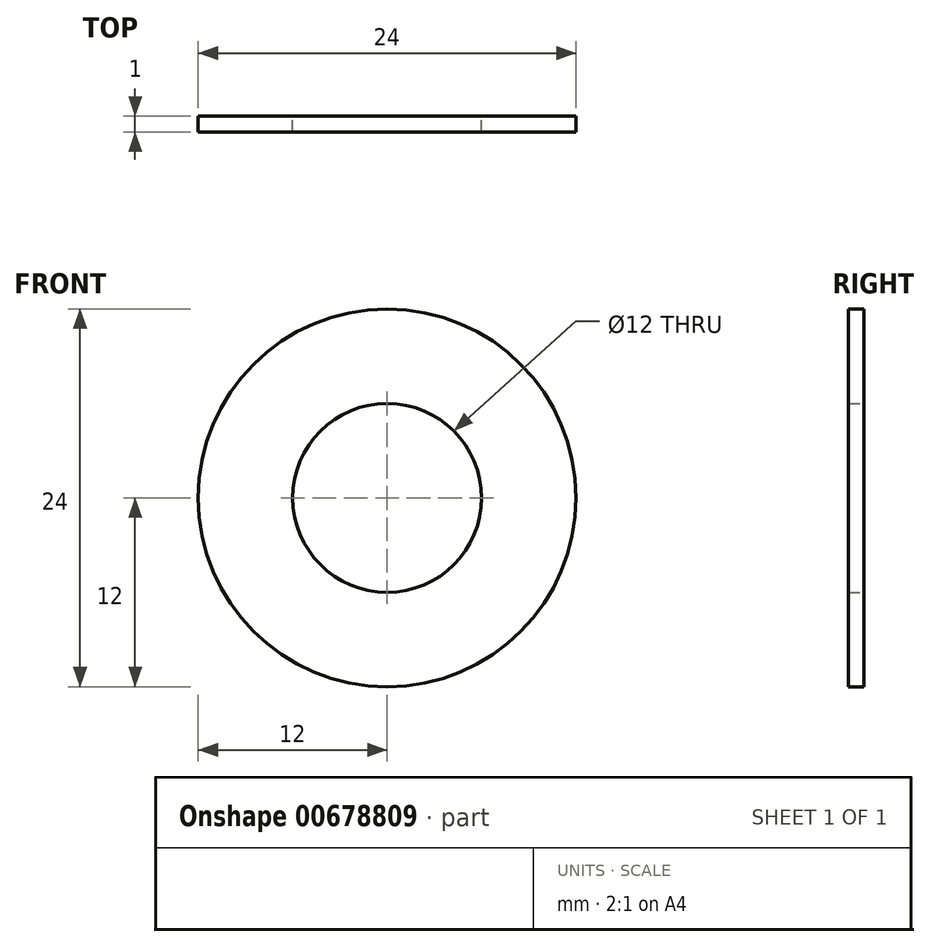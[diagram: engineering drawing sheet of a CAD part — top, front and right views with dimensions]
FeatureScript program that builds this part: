
annotation { "Feature Type Name" : "Feature", "Feature Type Description" : "" }
export const myFeature = defineFeature(function(context is Context, id is Id, definition is map)
    precondition{}
    {
        {
            var Q0;
            Q0=qCreatedBy(makeId("Front.planeOp"),FACE);
            var sketch = newSketch(context, id + "F0", { "sketchPlane" : qUnion([Q0])});
            skCircle(sketch, "E0", {"center": v(0, 0) * mm, "radius": 12 * mm});
            skCircle(sketch, "E1", {"center": v(0, 0) * mm, "radius": 6 * mm});
            skSolve(sketch);
        }
        {
            var Q0;
            Q0=makeQuery(id+"F0.imprint","IMPRINT",FACE,{"disambiguationData":[TD([[makeQuery(id+"F0.imprint","IMPRINT",EDGE,{"derivedFrom":sQuery(id+"F0.wireOp",EDGE,"E0")}),1.0]])]});
            extrude(context, id + "F1", {"entities" : qUnion([Q0]), "depth" : 1 * mm, "offsetDistance" : 25 * mm});
        }
    });
